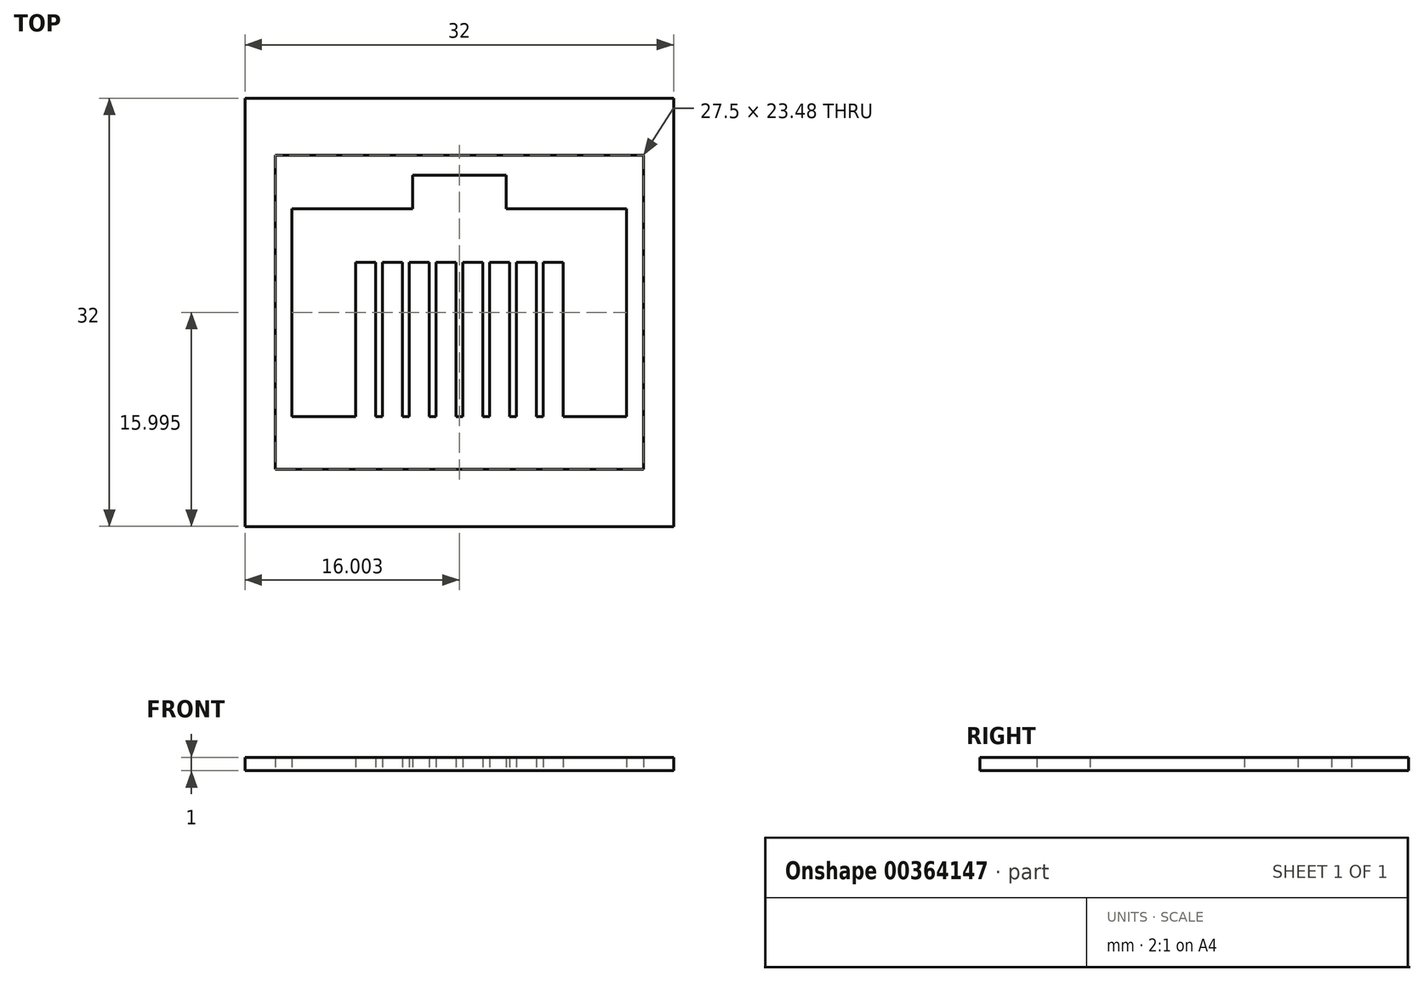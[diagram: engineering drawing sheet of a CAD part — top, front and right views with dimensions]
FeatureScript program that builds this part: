
annotation { "Feature Type Name" : "Feature", "Feature Type Description" : "" }
export const myFeature = defineFeature(function(context is Context, id is Id, definition is map)
    precondition{}
    {
        {
            var Q0;
            Q0=qCreatedBy(makeId("Top.planeOp"),FACE);
            var sketch = newSketch(context, id + "F0", { "sketchPlane" : qUnion([Q0])});
            skLineSegment(sketch, "E0", {"start": v(-0.01, 0) * mm, "end": v(0, 0.02) * mm});
            skLineSegment(sketch, "E1.bottom", {"start": v(16, -15.98) * mm, "end": v(-16, -15.98) * mm});
            skLineSegment(sketch, "E1.top", {"start": v(16, 16.02) * mm, "end": v(-16, 16.02) * mm});
            skLineSegment(sketch, "E1.left", {"start": v(16, -15.98) * mm, "end": v(16, 16.02) * mm});
            skLineSegment(sketch, "E1.right", {"start": v(-16, -15.98) * mm, "end": v(-16, 16.02) * mm});
            skPoint(sketch, "E1.middle", {"position": v(0, 0.02) * mm});
            skLineSegment(sketch, "E2.bottom", {"start": v(12.5, -7.77) * mm, "end": v(-12.5, -7.77) * mm});
            skLineSegment(sketch, "E2.left", {"start": v(12.5, -7.77) * mm, "end": v(12.5, 7.77) * mm});
            skLineSegment(sketch, "E2.right", {"start": v(-12.5, -7.77) * mm, "end": v(-12.5, 7.77) * mm});
            skPoint(sketch, "E2.middle", {"position": v(0, 0) * mm});
            skLineSegment(sketch, "E3.bottom", {"start": v(3.5, 10.27) * mm, "end": v(-3.5, 10.27) * mm});
            skLineSegment(sketch, "E3.left", {"start": v(3.5, 10.27) * mm, "end": v(3.5, 7.77) * mm});
            skLineSegment(sketch, "E3.right", {"start": v(-3.5, 10.27) * mm, "end": v(-3.5, 7.77) * mm});
            skPoint(sketch, "E3.middle", {"position": v(0, 7.77) * mm});
            skPoint(sketch, "E3.top.end.orphan", {"position": v(-3.5, 5.27) * mm});
            skPoint(sketch, "E4.orphan", {"position": v(3.5, 5.27) * mm});
            skLineSegment(sketch, "E5.left", {"start": v(-12.5, 7.77) * mm, "end": v(-12.5, 3.77) * mm});
            skLineSegment(sketch, "E5.right", {"start": v(12.5, 7.77) * mm, "end": v(12.5, 3.77) * mm});
            skLineSegment(sketch, "E6", {"start": v(-12.5, 7.77) * mm, "end": v(-3.5, 7.77) * mm});
            skLineSegment(sketch, "E7", {"start": v(12.5, 7.77) * mm, "end": v(3.5, 7.77) * mm});
            skLineSegment(sketch, "E8.bottom", {"start": v(-12.5, -7.77) * mm, "end": v(-9.75, -7.77) * mm});
            skLineSegment(sketch, "E8.left", {"start": v(-12.5, -7.77) * mm, "end": v(-12.5, 3.77) * mm});
            skLineSegment(sketch, "E9.top", {"start": v(12.5, -7.77) * mm, "end": v(9.75, -7.77) * mm});
            skLineSegment(sketch, "E9.left", {"start": v(12.5, 3.77) * mm, "end": v(12.5, -7.77) * mm});
            skLineSegment(sketch, "E10.bottom", {"start": v(-9.75, -7.77) * mm, "end": v(-8.25, -7.77) * mm});
            skLineSegment(sketch, "E11.bottom", {"start": v(-8.25, -7.77) * mm, "end": v(-7.75, -7.77) * mm});
            skLineSegment(sketch, "E11.right", {"start": v(-7.75, -7.77) * mm, "end": v(-7.75, 3.77) * mm});
            skLineSegment(sketch, "E12.bottom", {"start": v(-7.75, -7.77) * mm, "end": v(-6.25, -7.77) * mm});
            skLineSegment(sketch, "E12.top", {"start": v(-7.75, 3.77) * mm, "end": v(-6.25, 3.77) * mm});
            skLineSegment(sketch, "E12.right", {"start": v(-6.25, -7.77) * mm, "end": v(-6.25, 3.77) * mm});
            skLineSegment(sketch, "E13.bottom", {"start": v(-6.25, -7.77) * mm, "end": v(-5.75, -7.77) * mm});
            skLineSegment(sketch, "E13.right", {"start": v(-5.75, -7.77) * mm, "end": v(-5.75, 3.77) * mm});
            skLineSegment(sketch, "E14.bottom", {"start": v(-5.75, -7.77) * mm, "end": v(-4.25, -7.77) * mm});
            skLineSegment(sketch, "E14.top", {"start": v(-5.75, 3.77) * mm, "end": v(-4.25, 3.77) * mm});
            skLineSegment(sketch, "E14.right", {"start": v(-4.25, -7.77) * mm, "end": v(-4.25, 3.77) * mm});
            skLineSegment(sketch, "E15.bottom", {"start": v(-4.25, -7.77) * mm, "end": v(-3.75, -7.77) * mm});
            skLineSegment(sketch, "E15.right", {"start": v(-3.75, -7.77) * mm, "end": v(-3.75, 3.77) * mm});
            skLineSegment(sketch, "E16.bottom", {"start": v(-3.75, -7.77) * mm, "end": v(-2.25, -7.77) * mm});
            skLineSegment(sketch, "E16.top", {"start": v(-3.75, 3.77) * mm, "end": v(-2.25, 3.77) * mm});
            skLineSegment(sketch, "E16.right", {"start": v(-2.25, -7.77) * mm, "end": v(-2.25, 3.77) * mm});
            skLineSegment(sketch, "E17.bottom", {"start": v(-2.25, -7.77) * mm, "end": v(-1.75, -7.77) * mm});
            skLineSegment(sketch, "E17.right", {"start": v(-1.75, -7.77) * mm, "end": v(-1.75, 3.77) * mm});
            skLineSegment(sketch, "E18.bottom", {"start": v(-1.75, -7.77) * mm, "end": v(-0.25, -7.77) * mm});
            skLineSegment(sketch, "E18.top", {"start": v(-1.75, 3.77) * mm, "end": v(-0.25, 3.77) * mm});
            skLineSegment(sketch, "E18.right", {"start": v(-0.25, -7.77) * mm, "end": v(-0.25, 3.77) * mm});
            skLineSegment(sketch, "E19.bottom", {"start": v(-0.25, -7.77) * mm, "end": v(0.25, -7.77) * mm});
            skLineSegment(sketch, "E19.right", {"start": v(0.25, -7.77) * mm, "end": v(0.25, 3.77) * mm});
            skLineSegment(sketch, "E20.bottom", {"start": v(0.25, -7.77) * mm, "end": v(1.75, -7.77) * mm});
            skLineSegment(sketch, "E20.top", {"start": v(0.25, 3.77) * mm, "end": v(1.75, 3.77) * mm});
            skLineSegment(sketch, "E20.right", {"start": v(1.75, -7.77) * mm, "end": v(1.75, 3.77) * mm});
            skLineSegment(sketch, "E21.bottom", {"start": v(1.75, -7.77) * mm, "end": v(2.25, -7.77) * mm});
            skLineSegment(sketch, "E21.right", {"start": v(2.25, -7.77) * mm, "end": v(2.25, 3.77) * mm});
            skLineSegment(sketch, "E22.bottom", {"start": v(2.25, -7.77) * mm, "end": v(3.75, -7.77) * mm});
            skLineSegment(sketch, "E22.top", {"start": v(2.25, 3.77) * mm, "end": v(3.75, 3.77) * mm});
            skLineSegment(sketch, "E22.right", {"start": v(3.75, -7.77) * mm, "end": v(3.75, 3.77) * mm});
            skLineSegment(sketch, "E23.bottom", {"start": v(3.75, -7.77) * mm, "end": v(4.25, -7.77) * mm});
            skLineSegment(sketch, "E23.right", {"start": v(4.25, -7.77) * mm, "end": v(4.25, 3.77) * mm});
            skLineSegment(sketch, "E24.bottom", {"start": v(4.25, -7.77) * mm, "end": v(5.75, -7.77) * mm});
            skLineSegment(sketch, "E24.top", {"start": v(4.25, 3.77) * mm, "end": v(5.75, 3.77) * mm});
            skLineSegment(sketch, "E24.right", {"start": v(5.75, -7.77) * mm, "end": v(5.75, 3.77) * mm});
            skLineSegment(sketch, "E25.bottom", {"start": v(5.75, -7.77) * mm, "end": v(6.25, -7.77) * mm});
            skLineSegment(sketch, "E25.right", {"start": v(6.25, -7.77) * mm, "end": v(6.25, 3.77) * mm});
            skLineSegment(sketch, "E26.bottom", {"start": v(6.25, -7.77) * mm, "end": v(7.75, -7.77) * mm});
            skLineSegment(sketch, "E26.top", {"start": v(6.25, 3.77) * mm, "end": v(7.75, 3.77) * mm});
            skLineSegment(sketch, "E26.right", {"start": v(7.75, -7.77) * mm, "end": v(7.75, 3.77) * mm});
            skLineSegment(sketch, "E27.bottom", {"start": v(7.75, -7.77) * mm, "end": v(8.25, -7.77) * mm});
            skLineSegment(sketch, "E28.bottom", {"start": v(13.75, 11.76) * mm, "end": v(-13.75, 11.76) * mm});
            skLineSegment(sketch, "E28.top", {"start": v(13.75, -11.72) * mm, "end": v(-13.75, -11.72) * mm});
            skLineSegment(sketch, "E28.left", {"start": v(13.75, 11.76) * mm, "end": v(13.75, -11.72) * mm});
            skLineSegment(sketch, "E28.right", {"start": v(-13.75, 11.76) * mm, "end": v(-13.75, -11.72) * mm});
            skSolve(sketch);
        }
        {
            var Q0;
            Q0=makeQuery(id+"F0.imprint","IMPRINT",FACE,{"disambiguationData":[TD([[makeQuery(id+"F0.imprint","IMPRINT",EDGE,{"derivedFrom":sQuery(id+"F0.wireOp",EDGE,"E3.bottom")}),1.0]])]});
            extrude(context, id + "F1", {"entities" : qUnion([Q0]), "depth" : 1 * mm});
        }
        {
            var Q0;
            Q0=makeQuery(id+"F0.imprint","IMPRINT",FACE,{"disambiguationData":[TD([[makeQuery(id+"F0.imprint","IMPRINT",EDGE,{"derivedFrom":sQuery(id+"F0.wireOp",EDGE,"E1.bottom")}),-1.0]])]});
            extrude(context, id + "F2", {"entities" : qUnion([Q0]), "depth" : 1 * mm});
        }
        {
            var Q0;
            Q0=makeQuery(id+"F0.imprint","IMPRINT",FACE,{"disambiguationData":[TD([[makeQuery(id+"F0.imprint","IMPRINT",EDGE,{"derivedFrom":sQuery(id+"F0.wireOp",EDGE,"E10.bottom")}),1.0]])]});
            var Q1;
            Q1=makeQuery(id+"F0.imprint","IMPRINT",FACE,{"disambiguationData":[TD([[makeQuery(id+"F0.imprint","IMPRINT",EDGE,{"derivedFrom":sQuery(id+"F0.wireOp",EDGE,"E12.bottom")}),1.0]])]});
            var Q2;
            Q2=makeQuery(id+"F0.imprint","IMPRINT",FACE,{"disambiguationData":[TD([[makeQuery(id+"F0.imprint","IMPRINT",EDGE,{"derivedFrom":sQuery(id+"F0.wireOp",EDGE,"E14.bottom")}),1.0]])]});
            var Q3;
            Q3=makeQuery(id+"F0.imprint","IMPRINT",FACE,{"disambiguationData":[TD([[makeQuery(id+"F0.imprint","IMPRINT",EDGE,{"derivedFrom":sQuery(id+"F0.wireOp",EDGE,"E16.bottom")}),1.0]])]});
            var Q4;
            Q4=makeQuery(id+"F0.imprint","IMPRINT",FACE,{"disambiguationData":[TD([[makeQuery(id+"F0.imprint","IMPRINT",EDGE,{"derivedFrom":sQuery(id+"F0.wireOp",EDGE,"E18.bottom")}),1.0]])]});
            var Q5;
            Q5=makeQuery(id+"F0.imprint","IMPRINT",FACE,{"disambiguationData":[TD([[makeQuery(id+"F0.imprint","IMPRINT",EDGE,{"derivedFrom":sQuery(id+"F0.wireOp",EDGE,"E20.bottom")}),1.0]])]});
            var Q6;
            Q6=makeQuery(id+"F0.imprint","IMPRINT",FACE,{"disambiguationData":[TD([[makeQuery(id+"F0.imprint","IMPRINT",EDGE,{"derivedFrom":sQuery(id+"F0.wireOp",EDGE,"E22.bottom")}),1.0]])]});
            var Q7;
            Q7=makeQuery(id+"F0.imprint","IMPRINT",FACE,{"disambiguationData":[TD([[makeQuery(id+"F0.imprint","IMPRINT",EDGE,{"derivedFrom":sQuery(id+"F0.wireOp",EDGE,"E24.bottom")}),1.0]])]});
            var Q8;
            Q8=makeQuery(id+"F0.imprint","IMPRINT",FACE,{"disambiguationData":[TD([[makeQuery(id+"F0.imprint","IMPRINT",EDGE,{"derivedFrom":sQuery(id+"F0.wireOp",EDGE,"E26.bottom")}),1.0]])]});
            var Q9;
            Q9=makeQuery(id+"F0.imprint","IMPRINT",FACE,{"disambiguationData":[TD([[makeQuery(id+"F0.imprint","IMPRINT",EDGE,{"derivedFrom":sQuery(id+"F0.wireOp",EDGE,"E2.bottom")}),-1.0]])]});
            extrude(context, id + "F3", {"entities" : qUnion([Q0, Q1, Q2, Q3, Q4, Q5, Q6, Q7, Q8, Q9]), "depth" : 1 * mm});
        }
    });
